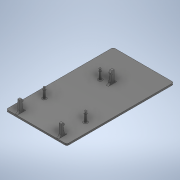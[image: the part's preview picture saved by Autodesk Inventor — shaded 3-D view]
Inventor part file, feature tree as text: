
AUTODESK INVENTOR PART (.ipt)
format: ipt  version: 2022 (Build 260153000, 153)  size: 219,136 bytes
history: native  units: mm
features: extrude x5, sketch x5, fillet x3, plane x2, mirror x1
ambient origin geometry x8: Origin, YZ Plane, XZ Plane, XY Plane, X Axis, Y Axis, Z Axis, Center Point
bodies: Solid1 (feature_tree)
feature tree (16):
  extrude  "Extrusion1"  Depth=127.0mm
  extrude  "Extrusion8"  Depth=3.0mm
  fillet  "Fillet3"  Radius=9.0mm
  extrude  "Extrusion9"  Depth=2.5mm
  fillet  "Fillet4"  Radius=2.5mm
  fillet  "Fillet5"  Radius=2.5mm
  plane  "Work Plane1"
  extrude  "Extrusion11"  Depth=0.5mm
  plane  "Work Plane2"
  mirror  "Mirror1"
  extrude  "Extrusion12"  Depth=0.5mm
  sketch  "Sketch1"  dims[d0=72.0mm d1=127.0mm]
  sketch  "Sketch2"  dims[d2=2.0mm d3=0.0mm d34=3.0mm d62=9.0mm d63=0.0mm]
  sketch  "Sketch8"  dims[d64=1.0mm d65=2.5mm d66=2.5mm d67=2.5mm]
  sketch  "Sketch10"  dims[d68=3.0mm d69=0.0mm d70=0.5mm]
  sketch  "Sketch11"  dims[d82=2.0mm d83=70.0mm d84=82.45mm d85=27.8mm d86=10.5mm d87=24.35mm d88=10.5mm d89=2.25mm d90=6.0mm d91=-11.5mm d92=10.0mm d96=1.0mm d98=3.0mm d100=2.5mm d102=1.5mm d103=3.0mm d105=2.5mm d106=0.0mm d107=10.0mm d109=2.5mm d112=3.0mm d113=3.0mm d115=2.5mm d116=0.0mm d117=10.9mm d118=1.0mm d119=1.5mm d120=10.9mm d121=0.5mm d122=82.45mm]
